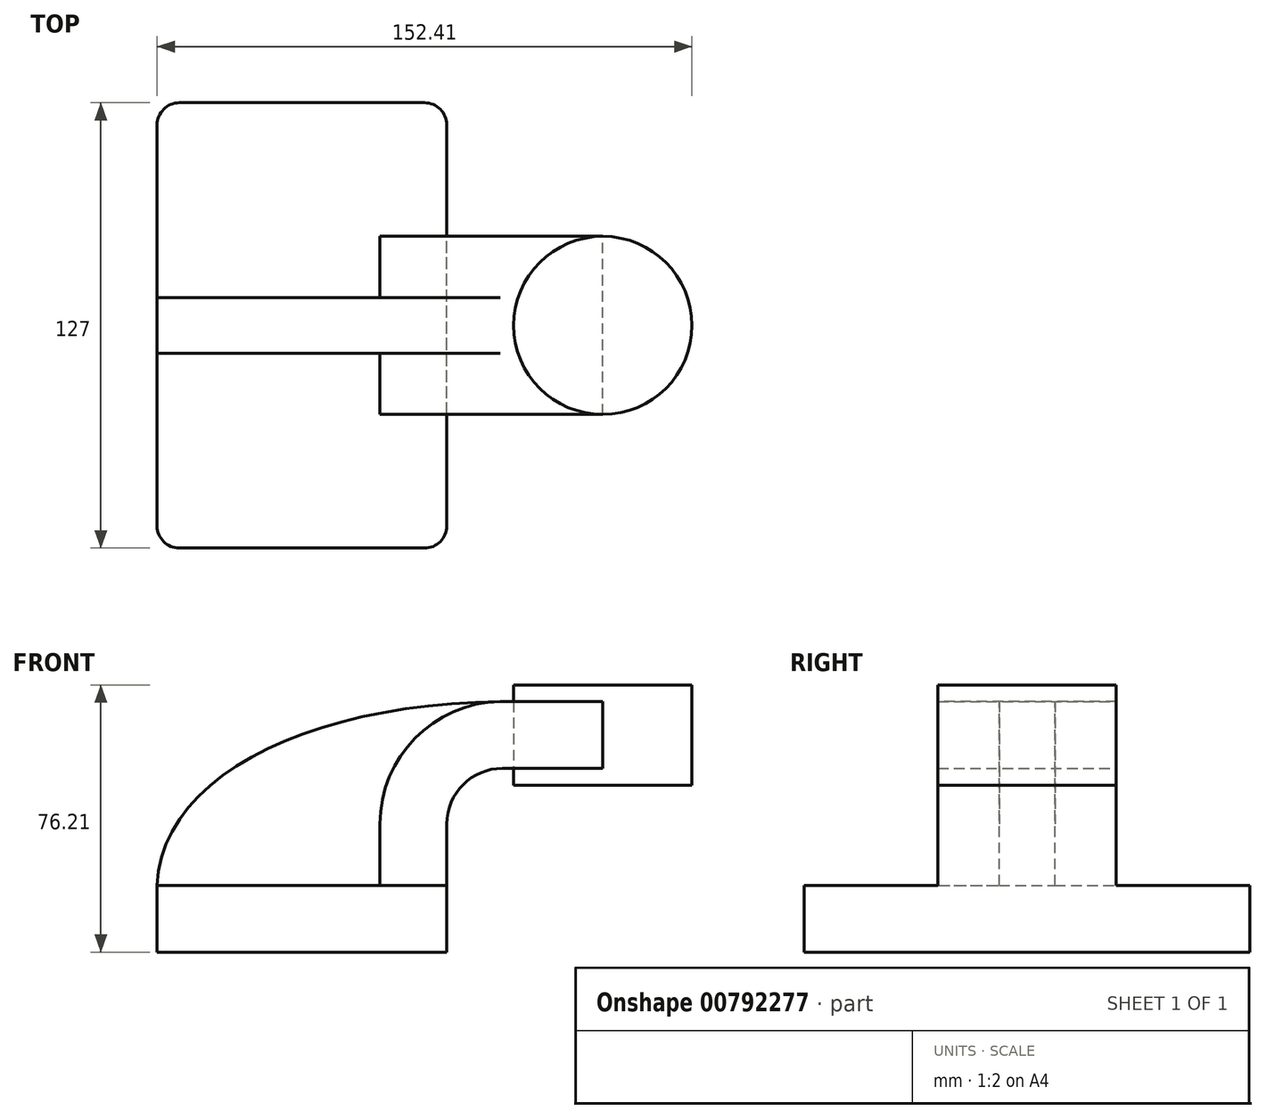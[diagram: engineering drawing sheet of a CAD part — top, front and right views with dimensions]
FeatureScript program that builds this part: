
annotation { "Feature Type Name" : "Feature", "Feature Type Description" : "" }
export const myFeature = defineFeature(function(context is Context, id is Id, definition is map)
    precondition{}
    {
        {
            var Q0;
            Q0=qCreatedBy(makeId("Front.planeOp"),FACE);
            var sketch = newSketch(context, id + "F0", { "sketchPlane" : qUnion([Q0])});
            skLineSegment(sketch, "E0.bottom", {"start": v(41.27, 9.53) * mm, "end": v(-41.28, 9.53) * mm});
            skLineSegment(sketch, "E0.top", {"start": v(41.28, -9.52) * mm, "end": v(-41.27, -9.52) * mm});
            skLineSegment(sketch, "E0.left", {"start": v(41.28, 9.53) * mm, "end": v(41.28, -9.52) * mm});
            skLineSegment(sketch, "E0.right", {"start": v(-41.28, 9.53) * mm, "end": v(-41.27, -9.52) * mm});
            skPoint(sketch, "E0.middle", {"position": v(0, 0) * mm});
            skLineSegment(sketch, "E1.bottom", {"start": v(111.12, 38.1) * mm, "end": v(60.32, 38.1) * mm});
            skLineSegment(sketch, "E1.top", {"start": v(111.12, 66.68) * mm, "end": v(60.32, 66.68) * mm});
            skLineSegment(sketch, "E1.left", {"start": v(111.12, 38.1) * mm, "end": v(111.12, 66.68) * mm});
            skLineSegment(sketch, "E1.right", {"start": v(60.32, 38.1) * mm, "end": v(60.32, 66.68) * mm});
            skPoint(sketch, "E1.middle", {"position": v(85.72, 52.39) * mm});
            skLineSegment(sketch, "E2", {"start": v(41.27, 9.53) * mm, "end": v(41.27, 27) * mm});
            skArc(sketch, "E3", {"start": v(41.27, 27) * mm, "mid": v(45.92, 38.23) * mm, "end": v(57.15, 42.88) * mm});
            skLineSegment(sketch, "E4", {"start": v(57.15, 42.88) * mm, "end": v(85.72, 42.88) * mm});
            skLineSegment(sketch, "E5.0", {"start": v(57.15, 61.93) * mm, "end": v(85.72, 61.93) * mm});
            skArc(sketch, "E5.1", {"start": v(22.23, 27) * mm, "mid": v(32.45, 51.7) * mm, "end": v(57.15, 61.93) * mm});
            skLineSegment(sketch, "E5.2", {"start": v(22.22, 9.53) * mm, "end": v(22.22, 27) * mm});
            skLineSegment(sketch, "E6", {"start": v(85.72, 38.1) * mm, "end": v(85.72, 66.68) * mm});
            skFitSpline(sketch, "E7", {"points": [v(-41.28, 9.52) * mm, v(57.15, 61.93) * mm], "startDerivative": vector(3.91, 94.55) * mm, "endDerivative": vector(162.93, 1.31) * mm});
            skSolve(sketch);
        }
        {
            var Q0;
            Q0=makeQuery(id+"F0.imprint","IMPRINT",FACE,{"disambiguationData":[TD([[makeQuery(id+"F0.imprint","IMPRINT",EDGE,{"derivedFrom":sQuery(id+"F0.wireOp",EDGE,"E0.top")}),-1.0]])]});
            extrude(context, id + "F1", {"entities" : qUnion([Q0]), "endBound" : BoundingType.SYMMETRIC, "depth" : 127 * mm, "offsetDistance" : 25.4 * mm});
        }
        {
            var Q0;
            {var subQ1=sQuery(id+"F0.wireOp",EDGE,"E2");Q0=makeQuery(id+"F0.imprint","IMPRINT",FACE,{"disambiguationData":[TD([[makeQuery(id+"F0.imprint","IMPRINT",EDGE,{"derivedFrom":subQ1}),1.0]])]});}
            var Q1;
            {var subQ0=sQuery(id+"F0.wireOp",EDGE,"E4");var subQ1=sQuery(id+"F0.wireOp",EDGE,"E1.right");var subQ2=makeQuery(id+"F0.imprint","INTERSECT",VERTEX,{"derivedFrom":[subQ1,subQ0]});Q1=makeQuery(id+"F0.imprint","IMPRINT",FACE,{"disambiguationData":[TD([[makeQuery(id+"F0.imprint","IMPRINT",EDGE,{"disambiguationData":[TD([[subQ2,-1.0]])],"derivedFrom":subQ1}),-1.0]])]});}
            extrude(context, id + "F2", {"entities" : qUnion([Q0, Q1]), "operationType" : NewBodyOperationType.ADD, "endBound" : BoundingType.SYMMETRIC, "depth" : 50.8 * mm, "offsetDistance" : 25.4 * mm});
        }
        {
            var Q0;
            {var subQ3=sQuery(id+"F0.wireOp",EDGE,"E5.2");Q0=makeQuery(id+"F0.imprint","IMPRINT",FACE,{"disambiguationData":[TD([[makeQuery(id+"F0.imprint","IMPRINT",EDGE,{"derivedFrom":subQ3}),1.0]])]});}
            extrude(context, id + "F3", {"entities" : qUnion([Q0]), "operationType" : NewBodyOperationType.ADD, "endBound" : BoundingType.SYMMETRIC, "depth" : 15.88 * mm, "offsetDistance" : 25.4 * mm});
        }
        {
            var Q0;
            {var subQ0=sQuery(id+"F0.wireOp",EDGE,"E1.left");Q0=makeQuery(id+"F0.imprint","IMPRINT",FACE,{"disambiguationData":[TD([[makeQuery(id+"F0.imprint","IMPRINT",EDGE,{"derivedFrom":subQ0}),1.0]])]});}
            var Q1;
            Q1=sQuery(id+"F0.wireOp",EDGE,"E6");
            revolve(context, id + "F4", {"surfaceOperationType" : NewSurfaceOperationType.NEW, "entities" : qUnion([Q0]), "axis" : qUnion([Q1]), "revolveType" : RevolveType.FULL});
        }
        {
            var Q0;
            Q0=makeQuery(id+"F1.opExtrude","CAP_EDGE",EDGE,{"disambiguationData":[OSD([sQuery(id+"F0.wireOp",EDGE,"E0.right")])],"isStart":false});
            var Q1;
            Q1=makeQuery(id+"F1.opExtrude","CAP_EDGE",EDGE,{"disambiguationData":[OSD([sQuery(id+"F0.wireOp",EDGE,"E0.left")])],"isStart":false});
            var Q2;
            Q2=makeQuery(id+"F1.opExtrude","CAP_EDGE",EDGE,{"disambiguationData":[OSD([sQuery(id+"F0.wireOp",EDGE,"E0.left")])],"isStart":true});
            var Q3;
            Q3=makeQuery(id+"F1.opExtrude","CAP_EDGE",EDGE,{"disambiguationData":[OSD([sQuery(id+"F0.wireOp",EDGE,"E0.right")])],"isStart":true});
            fillet(context, id + "F5", {"entities" : qUnion([Q0, Q1, Q2, Q3]), "radius" : 6.35 * mm, "tangentPropagation" : true, "allowEdgeOverflow" : false});
        }
    });
